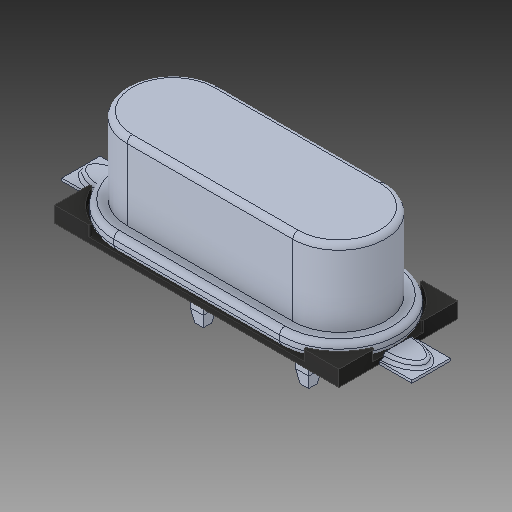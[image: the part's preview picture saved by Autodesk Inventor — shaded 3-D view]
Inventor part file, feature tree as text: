
AUTODESK INVENTOR PART (.ipt)
format: ipt  version: 2018.3 (Build 223284000, 284)  size: 284,160 bytes
history: native  units: mm
features: other x4, fillet x2, chamfer x1, mirror x1
ambient origin geometry x8: Origin, YZ Plane, XZ Plane, XY Plane, X Axis, Y Axis, Z Axis, Center Point
bodies: Body1 (feature_tree), Body2 (feature_tree), Body3 (feature_tree), Body4 (feature_tree)
feature tree (8):
  other  "Sólido1"
  other  "Sólido2"
  other  "Sólido3"
  other  "Sólido4"
  chamfer  "Chamfer1"  [1 undecoded]
  fillet  "Fillet2"  [1 undecoded]
  fillet  "Fillet3"  [1 undecoded]
  mirror  "Mirror1"
note: 3 required parameter values undecoded (feature->parameter linkage not recoverable at this tier; creation-order binding heuristic only, values carry confidence <= 0.55)
